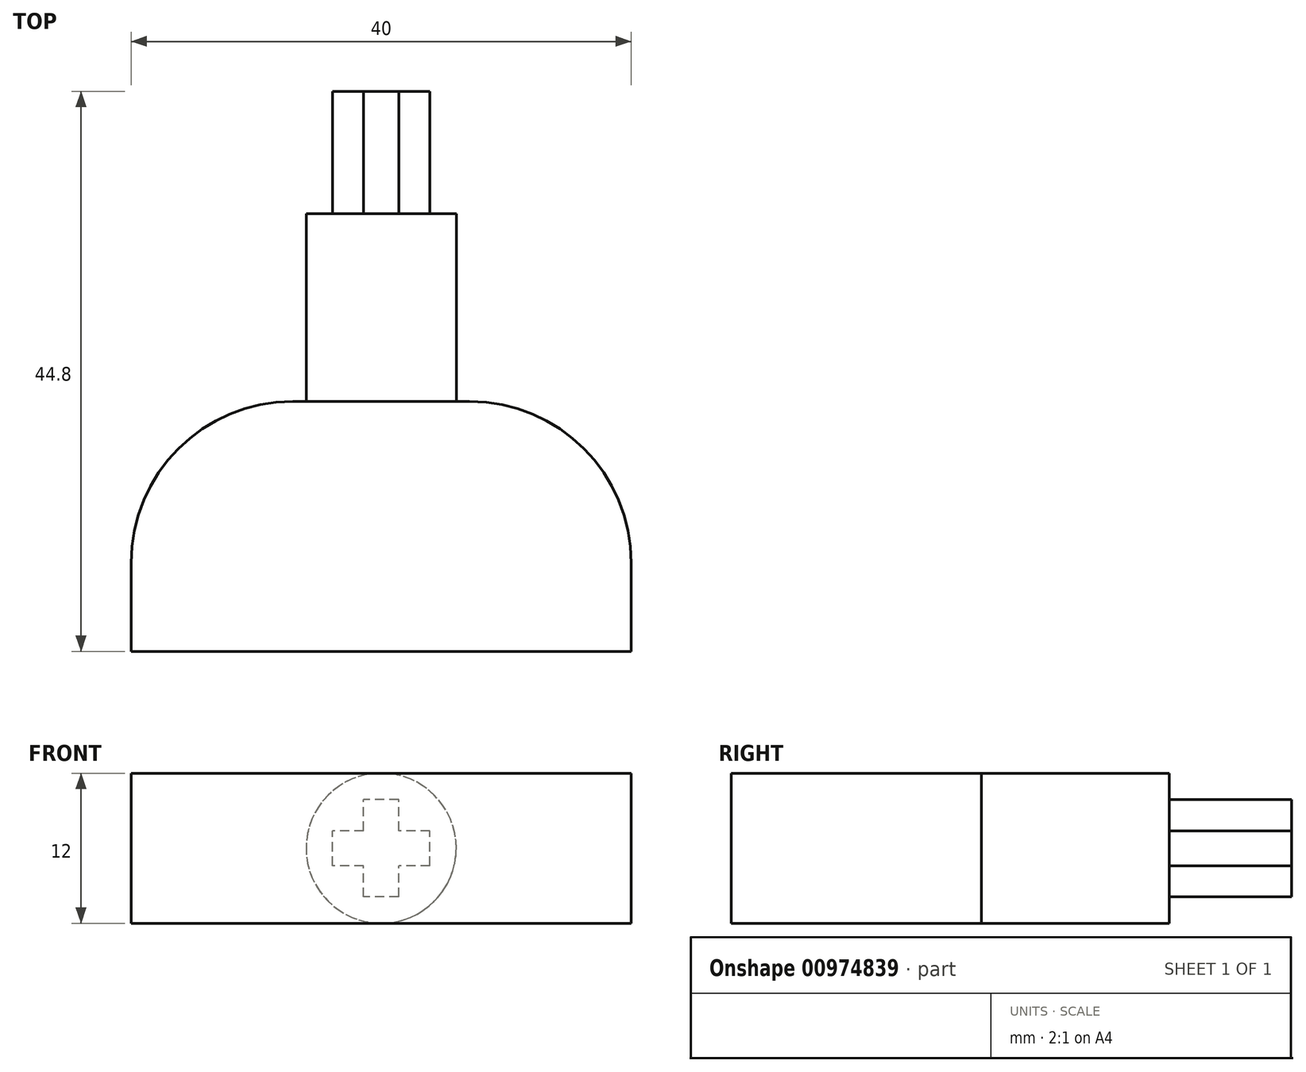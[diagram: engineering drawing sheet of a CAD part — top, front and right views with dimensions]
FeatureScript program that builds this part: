
annotation { "Feature Type Name" : "Feature", "Feature Type Description" : "" }
export const myFeature = defineFeature(function(context is Context, id is Id, definition is map)
    precondition{}
    {
        {
            var Q0;
            Q0=qCreatedBy(makeId("Top.planeOp"),FACE);
            var sketch = newSketch(context, id + "F0", { "sketchPlane" : qUnion([Q0])});
            skLineSegment(sketch, "E0.bottom", {"start": v(-7.08, -10) * mm, "end": v(7.08, -10) * mm});
            skLineSegment(sketch, "E0.top", {"start": v(-7.08, 10) * mm, "end": v(7.08, 10) * mm});
            skLineSegment(sketch, "E0.left", {"start": v(-20, -2.92) * mm, "end": v(-20, 2.92) * mm});
            skLineSegment(sketch, "E0.right", {"start": v(20, -2.92) * mm, "end": v(20, 2.92) * mm});
            skPoint(sketch, "E0.middle", {"position": v(0, 0) * mm});
            skPoint(sketch, "E1.visualSharp", {"position": v(-20, 10) * mm});
            skArc(sketch, "E1.filletArc", {"start": v(-7.08, 10) * mm, "mid": v(-16.22, 6.22) * mm, "end": v(-20, -2.92) * mm});
            skPoint(sketch, "E2.visualSharp", {"position": v(20, 10) * mm});
            skArc(sketch, "E2.filletArc", {"start": v(20, -2.92) * mm, "mid": v(16.22, 6.22) * mm, "end": v(7.08, 10) * mm});
            skPoint(sketch, "E3.visualSharp", {"position": v(20, -10) * mm});
            skPoint(sketch, "E4.visualSharp", {"position": v(-20, -10) * mm});
            skLineSegment(sketch, "E5", {"start": v(-20, 2.92) * mm, "end": v(-20, -10) * mm});
            skLineSegment(sketch, "E6", {"start": v(-7.08, -10) * mm, "end": v(20, -10) * mm});
            skLineSegment(sketch, "E7", {"start": v(-20, -10) * mm, "end": v(-7.08, -10) * mm});
            skLineSegment(sketch, "E8", {"start": v(20, 2.92) * mm, "end": v(20, -10) * mm});
            skSolve(sketch);
        }
        {
            var Q0;
            Q0 = qSketchRegion(id + "F0", true);
            extrude(context, id + "F1", {"entities" : qUnion([Q0]), "depth" : 12 * mm, "offsetDistance" : 25 * mm});
        }
        {
            var Q0;
            Q0=makeQuery(id+"F1.opExtrude","SWEPT_FACE",FACE,{"disambiguationData":[OSD([sQuery(id+"F0.wireOp",EDGE,"E0.top")])]});
            var sketch = newSketch(context, id + "F2", { "sketchPlane" : qUnion([Q0])});
            skCircle(sketch, "E9", {"center": v(0, 6) * mm, "radius": 6 * mm});
            skPoint(sketch, "E9.centerSnap0", {"position": v(-7.08, 6) * mm});
            skSolve(sketch);
        }
        {
            var Q0;
            {var subQ0=sQuery(id+"F2.wireOp",EDGE,"E9");var subQ1=sQuery(id+"F0.wireOp",EDGE,"E0.top");var subQ2=makeQuery(id+"F2.imprint","INTERSECT",VERTEX,{"derivedFrom":[makeQuery(id+"F1.opExtrude","CAP_EDGE",EDGE,{"disambiguationData":[OSD([subQ1])],"isStart":true}),subQ0]});Q0=makeQuery(id+"F2.imprint","IMPRINT",FACE,{"disambiguationData":[TD([[makeQuery(id+"F2.imprint","IMPRINT",EDGE,{"disambiguationData":[TD([[subQ2,1.0]])],"derivedFrom":subQ0}),1.0]])]});}
            extrude(context, id + "F3", {"entities" : qUnion([Q0]), "operationType" : NewBodyOperationType.ADD, "depth" : 15 * mm, "offsetDistance" : 25 * mm});
        }
        {
            var Q0;
            Q0=makeQuery(id+"F3.opExtrude","CAP_FACE",FACE,{"disambiguationData":[OSD([sQuery(id+"F2.wireOp",EDGE,"E9")])],"isStart":false});
            var sketch = newSketch(context, id + "F4", { "sketchPlane" : qUnion([Q0])});
            skLineSegment(sketch, "E10.bottom", {"start": v(-3.9, 4.6) * mm, "end": v(-1.4, 4.6) * mm});
            skLineSegment(sketch, "E10.top", {"start": v(-3.9, 7.4) * mm, "end": v(-1.4, 7.4) * mm});
            skLineSegment(sketch, "E10.left", {"start": v(-3.9, 4.6) * mm, "end": v(-3.9, 7.4) * mm});
            skLineSegment(sketch, "E10.right", {"start": v(3.9, 4.6) * mm, "end": v(3.9, 7.4) * mm});
            skPoint(sketch, "E10.middle", {"position": v(0, 6) * mm});
            skLineSegment(sketch, "E11.bottom", {"start": v(-1.4, 2.1) * mm, "end": v(1.4, 2.1) * mm});
            skLineSegment(sketch, "E11.top", {"start": v(-1.4, 9.9) * mm, "end": v(1.4, 9.9) * mm});
            skLineSegment(sketch, "E11.left", {"start": v(-1.4, 2.1) * mm, "end": v(-1.4, 4.6) * mm});
            skLineSegment(sketch, "E11.right", {"start": v(1.4, 2.1) * mm, "end": v(1.4, 4.6) * mm});
            skLineSegment(sketch, "E12.trimOffspring", {"start": v(1.4, 7.4) * mm, "end": v(3.9, 7.4) * mm});
            skLineSegment(sketch, "E13.trimOffspring", {"start": v(1.4, 7.4) * mm, "end": v(1.4, 9.9) * mm});
            skLineSegment(sketch, "E14.trimOffspring", {"start": v(-1.4, 7.4) * mm, "end": v(-1.4, 9.9) * mm});
            skLineSegment(sketch, "E15.trimOffspring", {"start": v(1.4, 4.6) * mm, "end": v(3.9, 4.6) * mm});
            skSolve(sketch);
        }
        {
            var Q0;
            Q0 = qSketchRegion(id + "F4", true);
            extrude(context, id + "F5", {"entities" : qUnion([Q0]), "operationType" : NewBodyOperationType.ADD, "depth" : 9.8 * mm, "offsetDistance" : 25 * mm});
        }
    });
